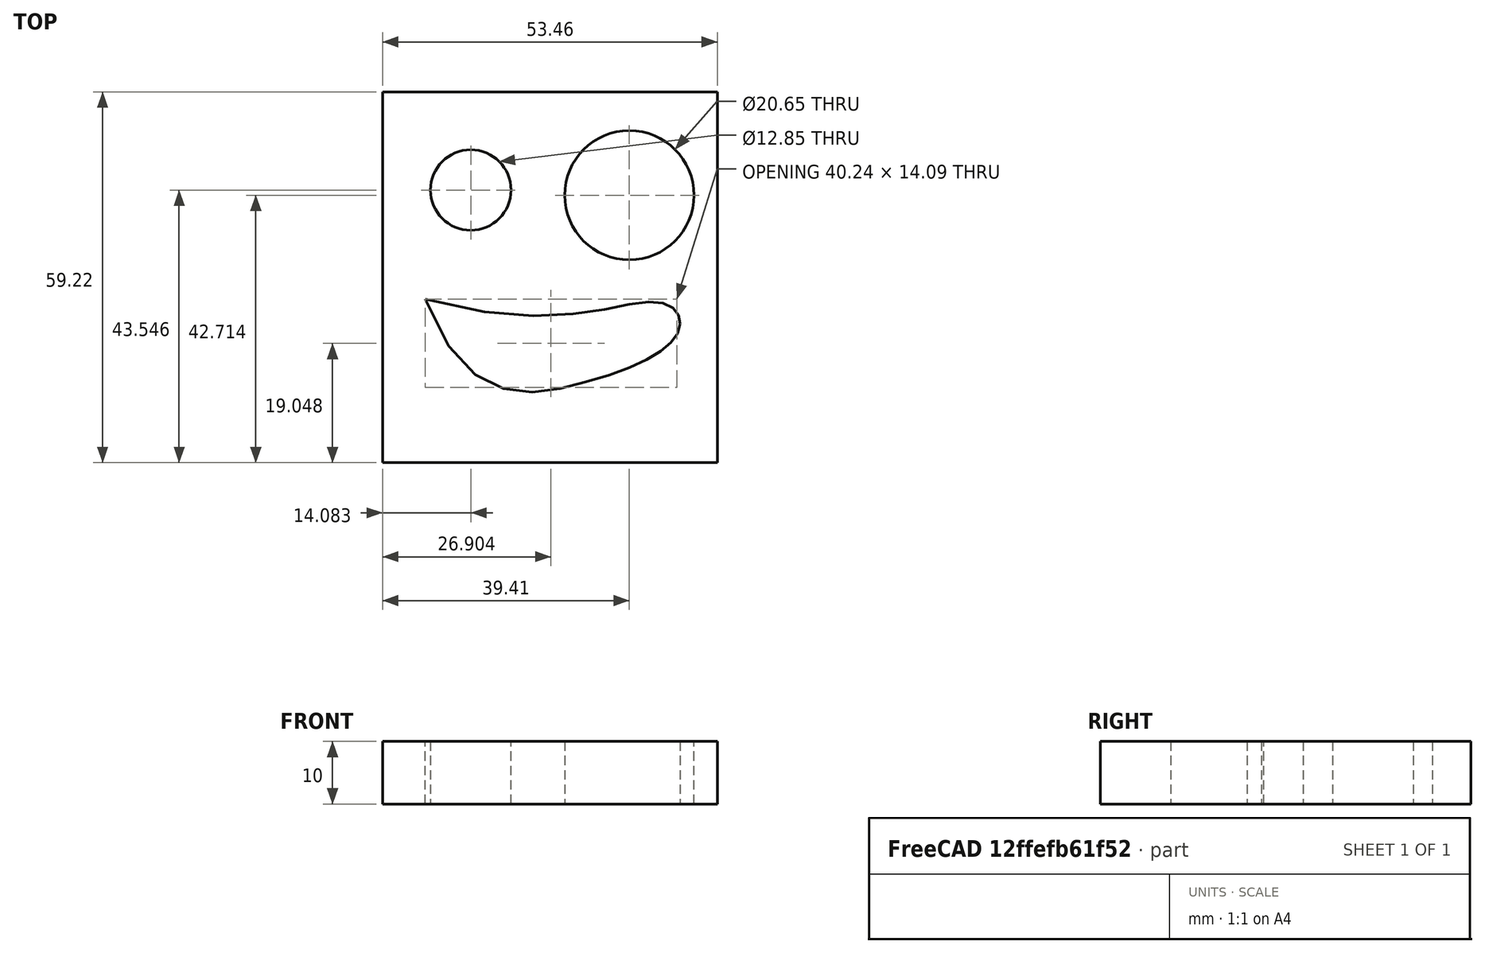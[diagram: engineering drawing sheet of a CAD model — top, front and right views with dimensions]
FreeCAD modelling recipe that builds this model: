
FCSTD DOCUMENT  (FreeCAD 0.20R29177 +426 (Git))
Label: cabeza_de_robot
License: Creative Commons Attribution-ShareAlike
LicenseURL: http://creativecommons.org/licenses/by-sa/4.0/
objects: Sketcher::SketchObject×1, Part::Extrusion×1
note: 2 computed .brp shape members not serialized (recipe doc carries the construction recipe); baked Part::Feature solids carry a one-line shape summary decoded from their .brp

FEATURE [Sketcher::SketchObject] Sketch
  FullyConstrained = false
  sketch-geometry (20):
    g0: LineSegment StartX=-26.7264 StartY=-27.2889 StartZ=0 EndX=-26.7264 EndY=31.9263 EndZ=0
    g1: LineSegment StartX=-26.7264 StartY=31.9263 StartZ=0 EndX=26.7264 EndY=31.9263 EndZ=0
    g2: LineSegment StartX=26.7264 StartY=31.9263 StartZ=0 EndX=26.7264 EndY=-27.2889 EndZ=0
    g3: LineSegment StartX=26.7264 StartY=-27.2889 StartZ=0 EndX=-26.7264 EndY=-27.2889 EndZ=0
    g4: GeomPoint X=0 Y=0 Z=0
    g5-g11: Circle x7 (B-spline internal-alignment scaffolding for g12; pole/knot coordinates omitted)
    g12: BSplineCurve PolesCount=7 KnotsCount=5 Degree=3 IsPeriodic=0
    g13-g17: GeomPoint x5 (B-spline internal-alignment scaffolding for g12; pole/knot coordinates omitted)
    g18: Circle CenterX=-12.6472 CenterY=16.256 CenterZ=0 NormalX=0 NormalY=0 NormalZ=1 AngleXU=0 Radius=6.42534
    g19: Circle CenterX=12.6798 CenterY=15.4236 CenterZ=0 NormalX=0 NormalY=0 NormalZ=1 AngleXU=0 Radius=10.325
  constraints (15):
    c: Coincident(g0,g1)
    c: Coincident(g1,g2)
    c: Coincident(g2,g3)
    c: Coincident(g3,g0)
    c: Horizontal(g3)
    c: Vertical(g0)
    c: Vertical(g2)
    c: Weight(g5) = 1
    c: Equal(g5,g6)
    c: PointOnObject(g6,g-2)
    c: Equal(g5, g7-g11) x5
    c: Coincident(g12,g5)
    c: InternalAlignment(g5-g11 -> g12) x7
    c: InternalAlignment(g13-g17 -> g12) x5
    c: Symmetric(g1,g0,g-2)
FEATURE [Part::Extrusion] Extrude
  Base = -> Sketch
  Dir = (0,0,1)
  DirMode = 2
  FaceMakerClass = Part::FaceMakerBullseye
  LengthFwd = 10
  LengthRev = 0
  Solid = true
  Symmetric = false
